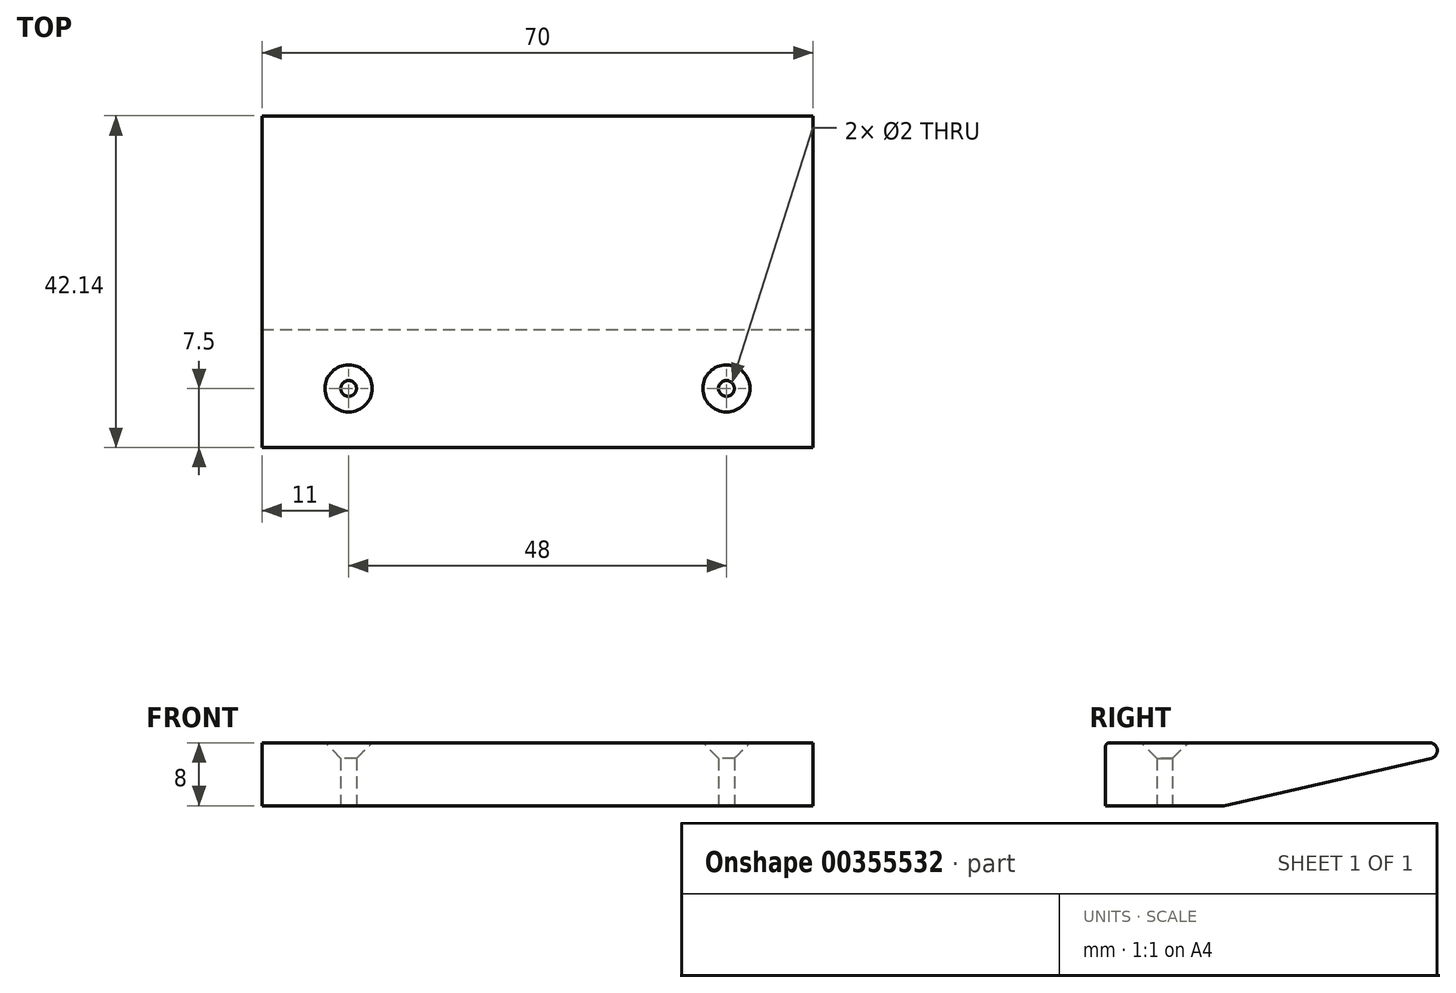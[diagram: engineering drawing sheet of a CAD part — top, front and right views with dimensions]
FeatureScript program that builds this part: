
annotation { "Feature Type Name" : "Feature", "Feature Type Description" : "" }
export const myFeature = defineFeature(function(context is Context, id is Id, definition is map)
    precondition{}
    {
        {
            var Q0;
            Q0=qCreatedBy(makeId("Top.planeOp"),FACE);
            var sketch = newSketch(context, id + "F0", { "sketchPlane" : qUnion([Q0])});
            skLineSegment(sketch, "E0.bottom", {"start": v(0, 0) * mm, "end": v(70, 0) * mm});
            skLineSegment(sketch, "E0.top", {"start": v(0, 15) * mm, "end": v(70, 15) * mm});
            skLineSegment(sketch, "E0.left", {"start": v(0, 0) * mm, "end": v(0, 15) * mm});
            skLineSegment(sketch, "E0.right", {"start": v(70, 0) * mm, "end": v(70, 15) * mm});
            skCircle(sketch, "E1", {"center": v(11, 7.5) * mm, "radius": 1 * mm});
            skCircle(sketch, "E2", {"center": v(59, 7.5) * mm, "radius": 1 * mm});
            skSolve(sketch);
        }
        {
            var Q0;
            Q0=makeQuery(id+"F0.imprint","IMPRINT",FACE,{"disambiguationData":[TD([[makeQuery(id+"F0.imprint","IMPRINT",EDGE,{"derivedFrom":sQuery(id+"F0.wireOp",EDGE,"E0.bottom")}),1.0]])]});
            extrude(context, id + "F1", {"entities" : qUnion([Q0]), "depth" : 8 * mm});
        }
        {
            var Q0;
            Q0=makeQuery(id+"F1.opExtrude","CAP_EDGE",EDGE,{"disambiguationData":[OSD([sQuery(id+"F0.wireOp",EDGE,"E1")])],"isStart":false});
            var Q1;
            Q1=makeQuery(id+"F1.opExtrude","CAP_EDGE",EDGE,{"disambiguationData":[OSD([sQuery(id+"F0.wireOp",EDGE,"E2")])],"isStart":false});
            chamfer(context, id + "F2", {"entities" : qUnion([Q0, Q1]), "width" : 2 * mm, "tangentPropagation" : true});
        }
        {
            var Q0;
            Q0=makeQuery(id+"F1.opExtrude","SWEPT_FACE",FACE,{"disambiguationData":[OSD([sQuery(id+"F0.wireOp",EDGE,"E0.right")])]});
            var sketch = newSketch(context, id + "F3", { "sketchPlane" : qUnion([Q0])});
            skLineSegment(sketch, "E3", {"start": v(15, 8) * mm, "end": v(50, 8) * mm});
            skLineSegment(sketch, "E4", {"start": v(15, 0) * mm, "end": v(50, 8) * mm});
            skSolve(sketch);
        }
        {
            var Q0;
            Q0=makeQuery(id+"F3.imprint","IMPRINT",FACE,{"disambiguationData":[TD([[makeQuery(id+"F3.imprint","IMPRINT",EDGE,{"derivedFrom":sQuery(id+"F3.wireOp",EDGE,"E3")}),-1.0]])]});
            extrude(context, id + "F4", {"entities" : qUnion([Q0]), "operationType" : NewBodyOperationType.ADD, "oppositeDirection" : true, "depth" : 70 * mm});
        }
        {
            var Q0;
            Q0=makeQuery(id+"F4.opExtrude","SWEPT_EDGE",EDGE,{"disambiguationData":[OSD([sQuery(id+"F3.wireOp",EDGE,"E3"),sQuery(id+"F3.wireOp",EDGE,"E4")])]});
            fillet(context, id + "F5", {"entities" : qUnion([Q0]), "radius" : 1 * mm, "tangentPropagation" : true, "allowEdgeOverflow" : false});
        }
        {
            var Q0;
            Q0=makeQuery(id+"F1.opExtrude","CAP_EDGE",EDGE,{"disambiguationData":[OSD([sQuery(id+"F0.wireOp",EDGE,"E0.bottom")])],"isStart":false});
            fillet(context, id + "F6", {"entities" : qUnion([Q0]), "radius" : 0.5 * mm, "tangentPropagation" : true, "allowEdgeOverflow" : false});
        }
    });
